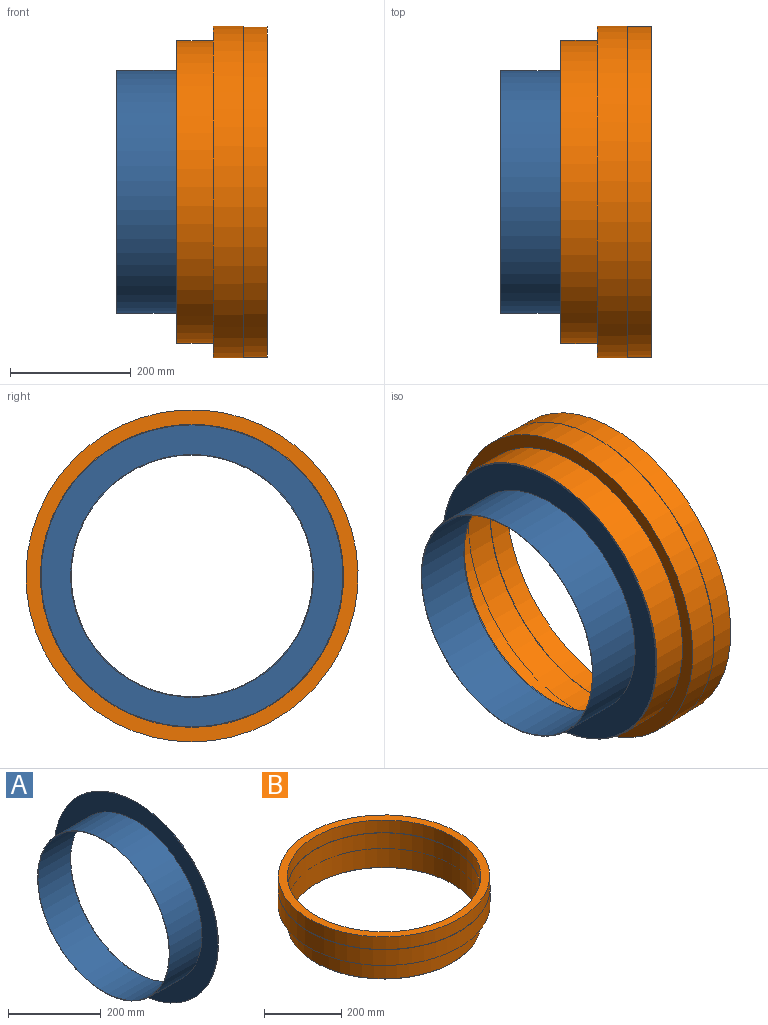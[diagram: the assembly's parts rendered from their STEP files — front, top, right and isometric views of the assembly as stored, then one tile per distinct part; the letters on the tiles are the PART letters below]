
ASSEMBLY  parts=2 mates=1
PART A: 6 faces, bbox 100x500x500 mm
  f0: cylinder r=200mm len=400mm, axis (-1,0,0), area 125663.7mm2, adj f1,f5
  f1: plane 500x500mm, normal (1,0,0), area 70685.8mm2, adj f0,f2
  f2: cylinder r=250mm len=500mm, axis (-1,0,0), area 1570.8mm2, adj f1,f3
  f3: plane 500x500mm, normal (-1,0,0), area 69426.1mm2, adj f2,f4
  f4: cylinder r=201mm len=402mm, axis (-1,0,0), area 125029.1mm2, adj f3,f5
  f5: plane 402x402mm, normal (-1,0,0), area 1259.8mm2, adj f0,f4
PART B: 10 faces, bbox 550x550x150 mm
  f0: plane 548x548mm, normal (0,0,1), area 37934.7mm2, adj f1,f9
  f1: cylinder r=274mm len=548mm, axis (0,0,1), area 68863.7mm2, adj f0,f2
  f2: plane 550x550mm, normal (0,0,1), area 1724.7mm2, adj f1,f3
  f3: cylinder r=275mm len=550mm, axis (0,0,1), area 86393.8mm2, adj f2,f4
  f4: plane 550x550mm, normal (0,0,-1), area 39659.5mm2, adj f3,f5
  f5: cylinder r=251mm len=502mm, axis (0,0,1), area 94624.8mm2, adj f4,f6
  f6: plane 502x502mm, normal (0,0,-1), area 1573.9mm2, adj f5,f7
  f7: cylinder r=250mm len=500mm, axis (0,0,1), area 172787.6mm2, adj f6,f8
  f8: plane 502x502mm, normal (0,0,1), area 1573.9mm2, adj f7,f9
  f9: cylinder r=251mm len=502mm, axis (0,0,1), area 63083.2mm2, adj f0,f8
PLACE A t=(384.11,1.5,21.17)mm fixed
PLACE B rot(axis=(0,1,0),90deg) t=(-272.49,1.5,21.17)mm
MATE fastened A.f0 <-> B.f1  axis (1,0,0) through (28.15,1.5,21.17)mm
